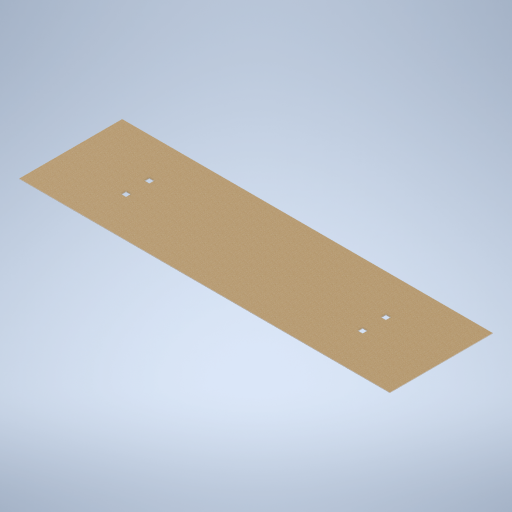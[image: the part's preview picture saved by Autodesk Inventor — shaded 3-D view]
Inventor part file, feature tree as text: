
AUTODESK INVENTOR PART (.ipt)
format: ipt  version: 2024.2 (Build 282272000, 272)  size: 340,480 bytes
history: native  units: mm
features: extrude x2, sketch x2
ambient origin geometry x8: Origin, YZ Plane, XZ Plane, XY Plane, X Axis, Y Axis, Z Axis, Center Point
bodies: Solid1 (feature_tree)
feature tree (4):
  extrude  "Extrusion1"  Depth=1500.0mm
  extrude  "Extrusion2"  Depth=40.0mm TaperAngle=0.0deg
  sketch  "Sketch1"  dims[d0=1500.0mm d1=1500.0mm]
  sketch  "Sketch2"  dims[d2=40.0mm d3=0.0mm d4=40.0mm d5=0.0mm]
